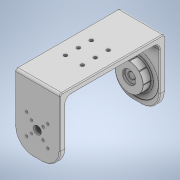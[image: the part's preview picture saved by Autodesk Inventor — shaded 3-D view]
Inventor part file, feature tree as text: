
AUTODESK INVENTOR PART (.ipt)
format: ipt  version: 2022 (Build 260153000, 153)  size: 534,016 bytes
history: native  units: mm
features: extrude x12, sketch x12, fillet x8, other x6, projected_geometry x3, mirror x1, pattern_circular x1, chamfer x1, revolve x1
ambient origin geometry x8: Origin, YZ Plane, XZ Plane, XY Plane, X Axis, Y Axis, Z Axis, Center Point
bodies: Body1 (feature_tree)
feature tree (45):
  other  "Твердое тело1"
  extrude  "Выдавливание1"  Depth=40.0mm
  extrude  "Выдавливание5"  Depth=93.4mm
  fillet  "Сопряжение3"  Radius=5.0mm
  other  "РабПлоскость1"
  extrude  "Выдавливание6"  Depth=45.8mm
  fillet  "Сопряжение4"  Radius=25.0mm
  fillet  "Сопряжение5"  Radius=3.0mm
  mirror  "Зеркальное отражение2"
  extrude  "Выдавливание7"  Depth=5.0mm
  other  "РабОсь6"
  extrude  "Выдавливание8"  Depth=55.0mm
  extrude  "Выдавливание9"  Depth=5.0mm TaperAngle=0.0deg
  extrude  "Выдавливание10"  Depth=5.0mm
  fillet  "Сопряжение7"  Radius=16.0mm
  other  "РабОсь1"
  pattern_circular  "Круговой массив1"  Count=4  [1 undecoded]
  fillet  "Сопряжение8"  Radius=7.0mm
  fillet  "Сопряжение11"  Radius=3.0mm
  other  "РабПлоскость3"
  extrude  "Выдавливание14"  Depth=37.8mm
  fillet  "Сопряжение14"  Radius=0.2mm
  extrude  "Выдавливание16"  Depth=24.7mm
  extrude  "Выдавливание17"  Depth=6.9mm TaperAngle=0.0deg
  fillet  "Сопряжение16"  Radius=0.4mm
  extrude  "Выдавливание18"  Depth=1.4mm TaperAngle=0.0deg
  chamfer  "Фаска2"  Distance=0.4mm
  other  "РабПлоскость4"
  revolve  "Вращение1"
  extrude  "Выдавливание19"  Depth=80.0mm TaperAngle=360.0deg
  sketch  "Эскиз1"
  sketch  "Эскиз5"
  sketch  "Эскиз6"
  sketch  "Эскиз7"
  projected_geometry  "Спроецированная петля1"
  sketch  "Эскиз9"
  sketch  "Эскиз10"
  sketch  "Эскиз17"
  sketch  "Эскиз19"
  sketch  "Эскиз20"
  projected_geometry  "Спроецированная петля3"
  sketch  "Эскиз21"
  sketch  "Эскиз22"
  sketch  "Эскиз23"
  projected_geometry  "Спроецированная петля4"
note: 1 required parameter value undecoded (feature->parameter linkage not recoverable at this tier; creation-order binding heuristic only, values carry confidence <= 0.55)
